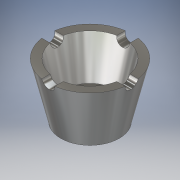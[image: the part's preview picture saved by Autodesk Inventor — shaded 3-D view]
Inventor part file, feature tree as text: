
AUTODESK INVENTOR PART (.ipt)
format: ipt  version: 2018 (Build 220112000, 112)  size: 158,208 bytes
history: native  units: in
note: dims shown in document units (in); Inventor stores cm internally (conversion verified against a paired STEP export)
features: sketch x3, extrude x2, revolve x1
ambient origin geometry x8: Origin, YZ Plane, XZ Plane, XY Plane, X Axis, Y Axis, Z Axis, Center Point
bodies: Solid1 (feature_tree)
feature tree (6):
  revolve  "Revolution1"  [1 undecoded]
  extrude  "Extrusion1"  Depth=0.4724in
  extrude  "Extrusion2"  Depth=0.3937in
  sketch  "Sketch1"  dims[d0=0.4528in d1=0.4331in]
  sketch  "Sketch2"  dims[d2=0.8858in d3=0.4724in]
  sketch  "Sketch3"  dims[d4=0.748in d5=0.315in d7=0.2435in d8=1.2795in d9=1.6535in d10=90.0deg d11=0.3937in d12=0.3937in d13=0.0in d14=0.3937in d15=0.3937in d16=0.0in]
note: 1 required parameter value undecoded (feature->parameter linkage not recoverable at this tier; creation-order binding heuristic only, values carry confidence <= 0.55)
